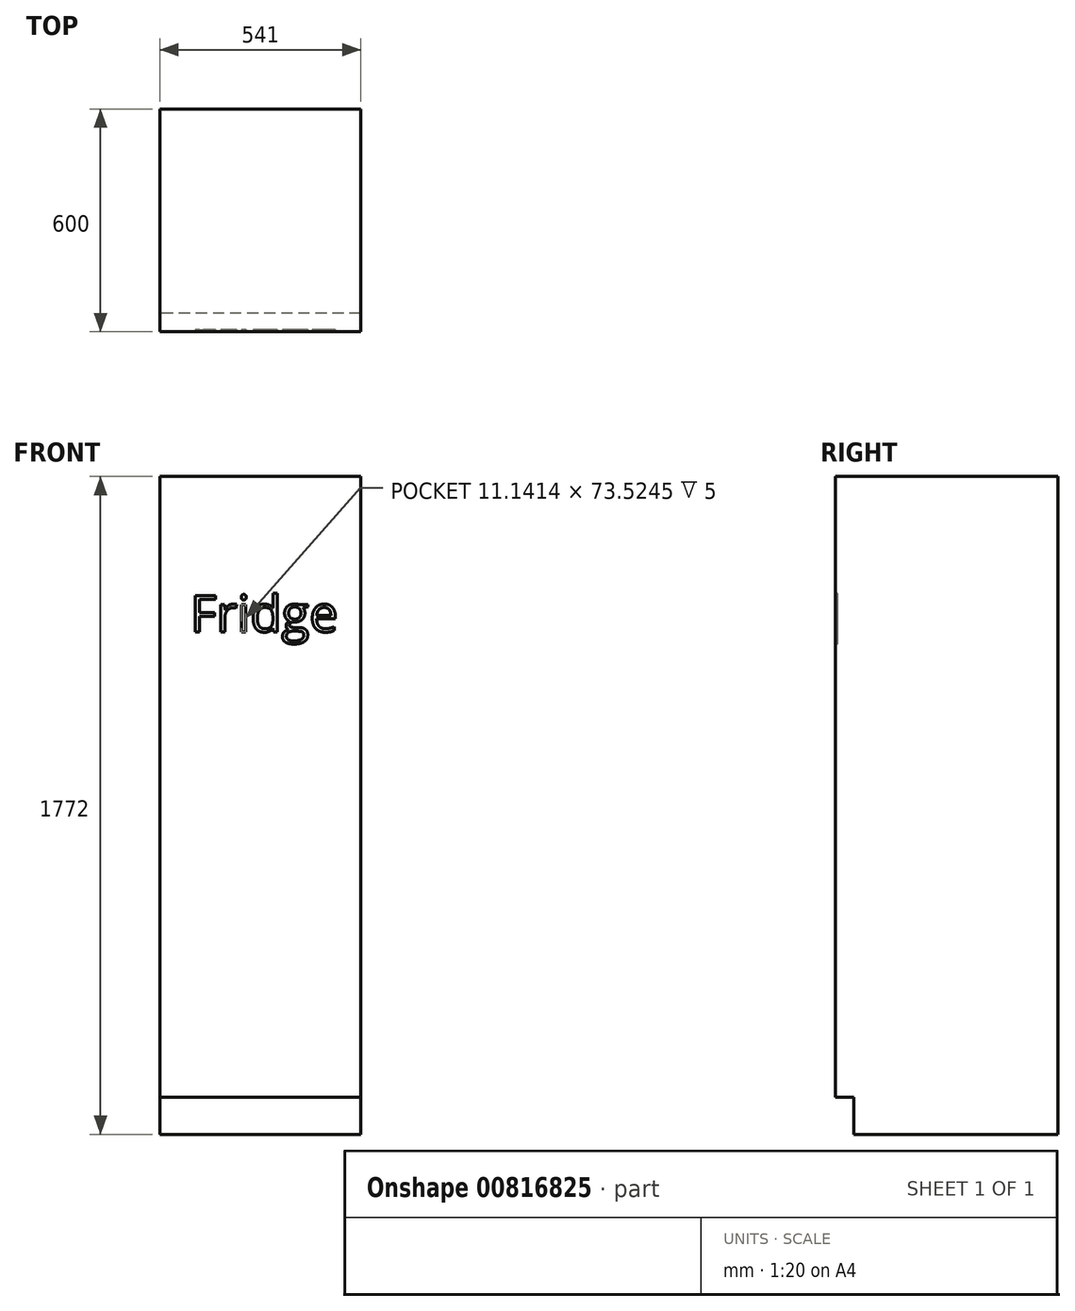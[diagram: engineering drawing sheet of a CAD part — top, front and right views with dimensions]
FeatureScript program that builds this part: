
annotation { "Feature Type Name" : "Feature", "Feature Type Description" : "" }
export const myFeature = defineFeature(function(context is Context, id is Id, definition is map)
    precondition{}
    {
        {
            var Q0;
            Q0=qCreatedBy(makeId("Front.planeOp"),FACE);
            var sketch = newSketch(context, id + "F0", { "sketchPlane" : qUnion([Q0])});
            skLineSegment(sketch, "E0.bottom", {"start": v(0, 0) * mm, "end": v(-541, 0) * mm});
            skLineSegment(sketch, "E0.top", {"start": v(0, 1672) * mm, "end": v(-541, 1672) * mm});
            skLineSegment(sketch, "E0.left", {"start": v(0, 0) * mm, "end": v(0, 1672) * mm});
            skLineSegment(sketch, "E0.right", {"start": v(-541, 0) * mm, "end": v(-541, 1672) * mm});
            skSolve(sketch);
        }
        {
            var Q0;
            Q0=makeQuery(id+"F0.imprint","IMPRINT",FACE,{"disambiguationData":[TD([[makeQuery(id+"F0.imprint","IMPRINT",EDGE,{"derivedFrom":sQuery(id+"F0.wireOp",EDGE,"E0.bottom")}),-1.0]])]});
            extrude(context, id + "F1", {"entities" : qUnion([Q0]), "depth" : 600 * mm, "offsetDistance" : 25 * mm});
        }
        {
            var Q0;
            Q0=qCreatedBy(makeId("Front.planeOp"),FACE);
            var sketch = newSketch(context, id + "F2", { "sketchPlane" : qUnion([Q0])});
            skLineSegment(sketch, "E1.bottom", {"start": v(0, 0) * mm, "end": v(-541, 0) * mm});
            skLineSegment(sketch, "E1.top", {"start": v(0, -100) * mm, "end": v(-541, -100) * mm});
            skLineSegment(sketch, "E1.left", {"start": v(0, 0) * mm, "end": v(0, -100) * mm});
            skLineSegment(sketch, "E1.right", {"start": v(-541, 0) * mm, "end": v(-541, -100) * mm});
            skSolve(sketch);
        }
        {
            var Q0;
            Q0=qSketchRegion(id+"F2",true);
            extrude(context, id + "F3", {"entities" : qUnion([Q0]), "operationType" : NewBodyOperationType.ADD, "depth" : 550 * mm, "offsetDistance" : 25 * mm});
        }
        {
            var Q0;
            Q0=makeQuery(id+"F1.opExtrude","CAP_FACE",FACE,{"disambiguationData":[OSD([sQuery(id+"F0.wireOp",EDGE,"E0.bottom"),sQuery(id+"F0.wireOp",EDGE,"E0.top"),sQuery(id+"F0.wireOp",EDGE,"E0.left"),sQuery(id+"F0.wireOp",EDGE,"E0.right")])],"isStart":false});
            var sketch = newSketch(context, id + "F4", { "sketchPlane" : qUnion([Q0])});
            skText(sketch, "E2", { "text": "Fridge", "fontName": "OpenSans-Regular.ttf"});
            const initialGuessF4  = {"E2": [-0.45963, 1.25363, 1, 0, 0.09892]};
            skSetInitialGuess(sketch, initialGuessF4);
            skSolve(sketch);
        }
        {
            var Q0;
            Q0 = qSketchRegion(id + "F4", true);
            extrude(context, id + "F5", {"entities" : qUnion([Q0]), "operationType" : NewBodyOperationType.REMOVE, "oppositeDirection" : true, "depth" : 5 * mm, "offsetDistance" : 25 * mm});
        }
    });
